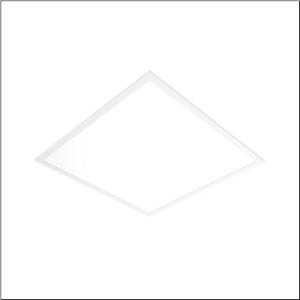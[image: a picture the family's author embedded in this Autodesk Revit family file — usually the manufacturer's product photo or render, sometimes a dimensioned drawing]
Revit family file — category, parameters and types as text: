
# Revit family: apollon_r__41_51mh11w72422_84d9
name_source: partatom
category: Lighting Fixtures
units: mm (PartAtom-declared; Revit-internal decimal feet)

## family parameters
Cut with Voids When Loaded = No
Host = Face
Light Source = No
Part Type = Normal
Room Calculation Point = No
Round Connector Dimension = Use Diameter
Shared = No

## types (1)
- Apollon® 41 (1 x LED, 3700 lm, 35 W, 4000K)
    Apparent Load = 35 VA
    CIE Flux Codes = 62 87 97 100 100
    Color Rendering = 80
    Color Temperature = 4000K
    Default Elevation = 1800 mm
    Description = Apollon® 41, office luminaire, primary optical cover: prismatic diffuser, of PS, light emission: direct distribution, primary light characteristic: symmetric, installation type: lay-in mounting, LED, rated luminous flux: 3.700lm, luminous efficacy: 105lm/W, light colour: 840, colour temperature: 4000K, control gear: ECG, with terminal, 3-pole, mains connection: 220..240V, AC, 50/60Hz, rated input power: 35W, housing, of aluminium section, traffic white (RAL 9016), module: M625, length: 620mm, width: 620mm, height: 32mm, housing upper side, of sheet steel, protection rating (complete): IP20, protection rating (lamp compartment, on room side): IP40, insulation class (complete): insulation class II (safety insulation), certification: CE, ENEC, permissible operating ambient temperature: -20..+40°C, packaging unit: 1 piece
    Height = 0 mm  [stored 0 ft]
    Lamp = 1 x LED
    Lamp Light Flux = 3700 lm
    Lamp Power = 35 W
    Lamp count = 1
    Length = 620 mm
    Luminous efficacy = 106 lm/W
    Manufacturer = Siteco
    ModVariant = No
    Model = 51MH11W72422
    Mounting Place = Ceiling
    Mounting Type = Recessed
    Number of Poles = 1
    OnlyDefault = Yes
    Power Factor = 1
    Product Name = Apollon® 41
    Product group = office luminaire | ceiling recessed
    ProductGroupID = 401
    Protection Class = Protection class II
    Protection Degree = IP 20
    RLX_Detail_Level = 1
    RLX_Emergency_Light_Flux = 0 lm
    RLX_Emergency_Type = 0
    RLX_Emergency_Type_DB = No
    RlxData = <blob elided: 14873 chars, md5=4809fb77>
    Socket = socket
    Standby Power = 0 W
    System Light Flux = 3700 lm
    System Power = 35 W
    Type Comments = Product without accessories
    Type Image = l_1291024.jpg
    URL = http://relux.com
    VarID = ---
    Voltage = 0 V
    Weight = 0.00 kg
    Width = 620 mm

note: [stored X ft] marks values corroborated as IEEE doubles in the binary element streams (Revit-internal decimal feet)

## geometry (parser evidence)
native form markers: Sweep x11
no freeform markers — native parametric forms only
